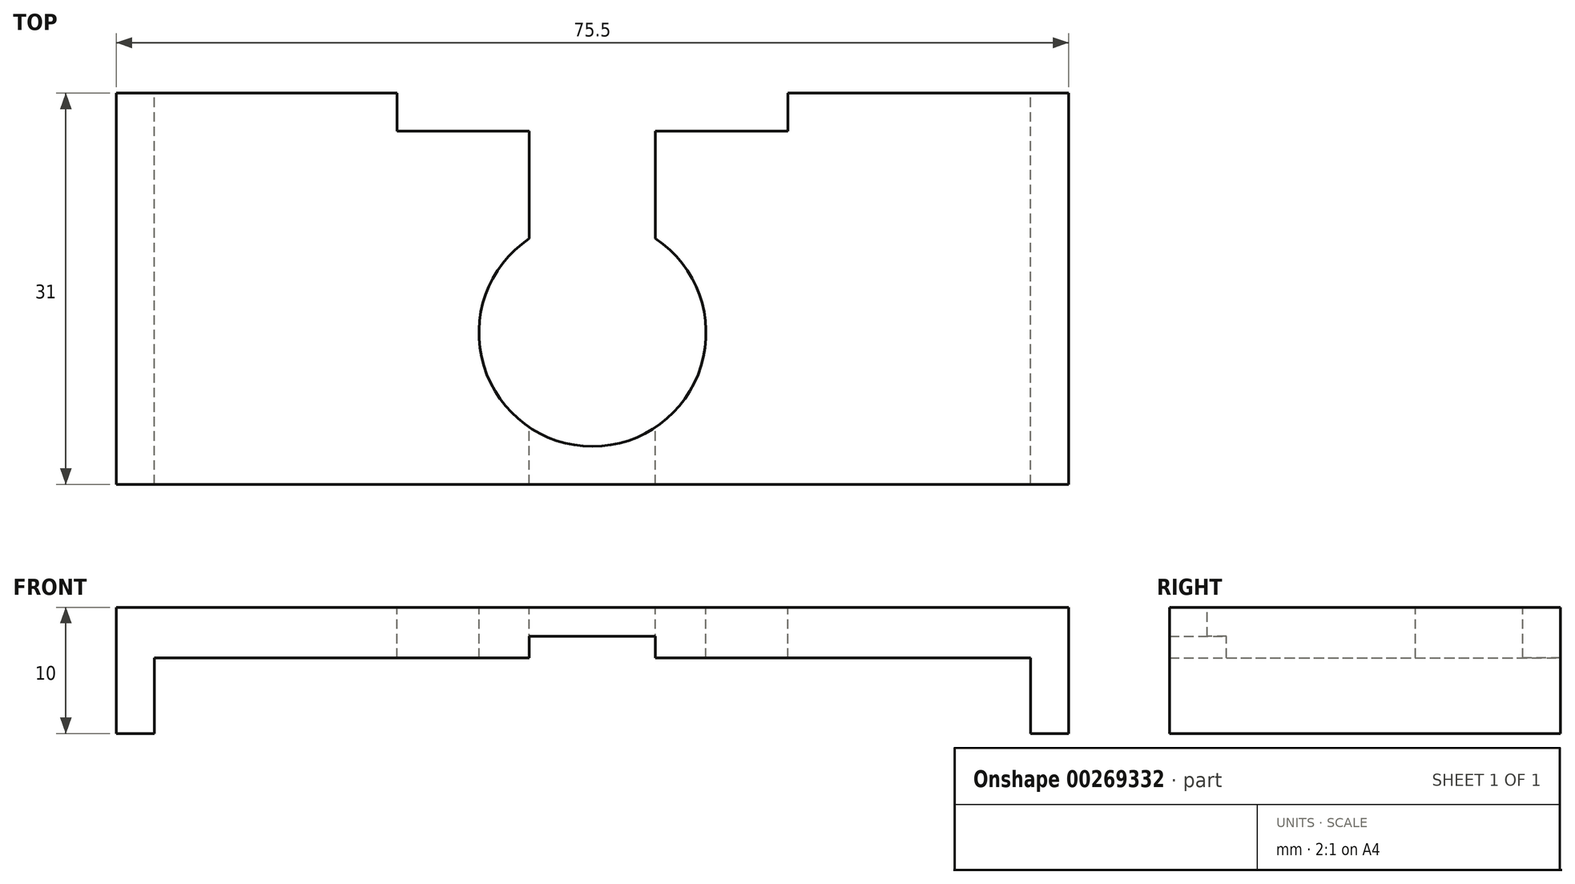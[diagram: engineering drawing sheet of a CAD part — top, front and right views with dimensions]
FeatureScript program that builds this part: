
annotation { "Feature Type Name" : "Feature", "Feature Type Description" : "" }
export const myFeature = defineFeature(function(context is Context, id is Id, definition is map)
    precondition{}
    {
        {
            var Q0;
            Q0=qCreatedBy(makeId("Front.planeOp"),FACE);
            var sketch = newSketch(context, id + "F0", { "sketchPlane" : qUnion([Q0])});
            skLineSegment(sketch, "E0", {"start": v(-37.75, 0) * mm, "end": v(37.75, 0) * mm});
            skLineSegment(sketch, "E1", {"start": v(37.75, 0) * mm, "end": v(37.75, -10) * mm});
            skLineSegment(sketch, "E2", {"start": v(37.75, -10) * mm, "end": v(34.75, -10) * mm});
            skLineSegment(sketch, "E3", {"start": v(34.75, -10) * mm, "end": v(34.75, -4) * mm});
            skLineSegment(sketch, "E4", {"start": v(34.75, -4) * mm, "end": v(5, -4) * mm});
            skLineSegment(sketch, "E5", {"start": v(-34.75, -4) * mm, "end": v(-34.75, -10) * mm});
            skLineSegment(sketch, "E6", {"start": v(-34.75, -10) * mm, "end": v(-37.75, -10) * mm});
            skLineSegment(sketch, "E7", {"start": v(-37.75, -10) * mm, "end": v(-37.75, 0) * mm});
            skLineSegment(sketch, "E8", {"start": v(-5, -4) * mm, "end": v(-5, -2.3) * mm});
            skLineSegment(sketch, "E9", {"start": v(-5, -2.3) * mm, "end": v(5, -2.3) * mm});
            skLineSegment(sketch, "E10", {"start": v(5, -2.3) * mm, "end": v(5, -4) * mm});
            skLineSegment(sketch, "E11.trimOffspring", {"start": v(-5, -4) * mm, "end": v(-34.75, -4) * mm});
            skLineSegment(sketch, "E12", {"start": v(0, 0) * mm, "end": v(0, -2.3) * mm, "construction": true});
            skSolve(sketch);
        }
        {
            var Q0;
            Q0=makeQuery(id+"F0.imprint","IMPRINT",FACE,{"disambiguationData":[TD([[makeQuery(id+"F0.imprint","IMPRINT",EDGE,{"derivedFrom":sQuery(id+"F0.wireOp",EDGE,"E0")}),-1.0]])]});
            extrude(context, id + "F1", {"entities" : qUnion([Q0]), "depth" : 31 * mm});
        }
        {
            var Q0;
            Q0=makeQuery(id+"F1.opExtrude","SWEPT_FACE",FACE,{"disambiguationData":[OSD([sQuery(id+"F0.wireOp",EDGE,"E0")])]});
            var sketch = newSketch(context, id + "F2", { "sketchPlane" : qUnion([Q0])});
            skLineSegment(sketch, "E13", {"start": v(-15.5, 0) * mm, "end": v(-15.5, -3) * mm});
            skLineSegment(sketch, "E14", {"start": v(-15.5, -3) * mm, "end": v(-5, -3) * mm});
            skLineSegment(sketch, "E15", {"start": v(15.5, -3) * mm, "end": v(15.5, 0) * mm});
            skLineSegment(sketch, "E16", {"start": v(0, 0) * mm, "end": v(0, -19) * mm, "construction": true});
            skArc(sketch, "E17", {"start": v(-5, -11.52) * mm, "mid": v(0, -28) * mm, "end": v(5, -11.52) * mm});
            skLineSegment(sketch, "E18", {"start": v(-5, -3) * mm, "end": v(-5, -11.52) * mm});
            skLineSegment(sketch, "E19", {"start": v(5, -3) * mm, "end": v(5, -11.52) * mm});
            skLineSegment(sketch, "E20.trimOffspring", {"start": v(5, -3) * mm, "end": v(15.5, -3) * mm});
            skSolve(sketch);
        }
        {
            var Q0;
            {var subQ0=sQuery(id+"F2.wireOp",EDGE,"E13");Q0=makeQuery(id+"F2.imprint","IMPRINT",FACE,{"disambiguationData":[TD([[makeQuery(id+"F2.imprint","IMPRINT",EDGE,{"derivedFrom":subQ0}),1.0]])]});}
            extrude(context, id + "F3", {"entities" : qUnion([Q0]), "operationType" : NewBodyOperationType.REMOVE, "endBound" : BoundingType.UP_TO_NEXT, "oppositeDirection" : true, "depth" : 25 * mm});
        }
    });
